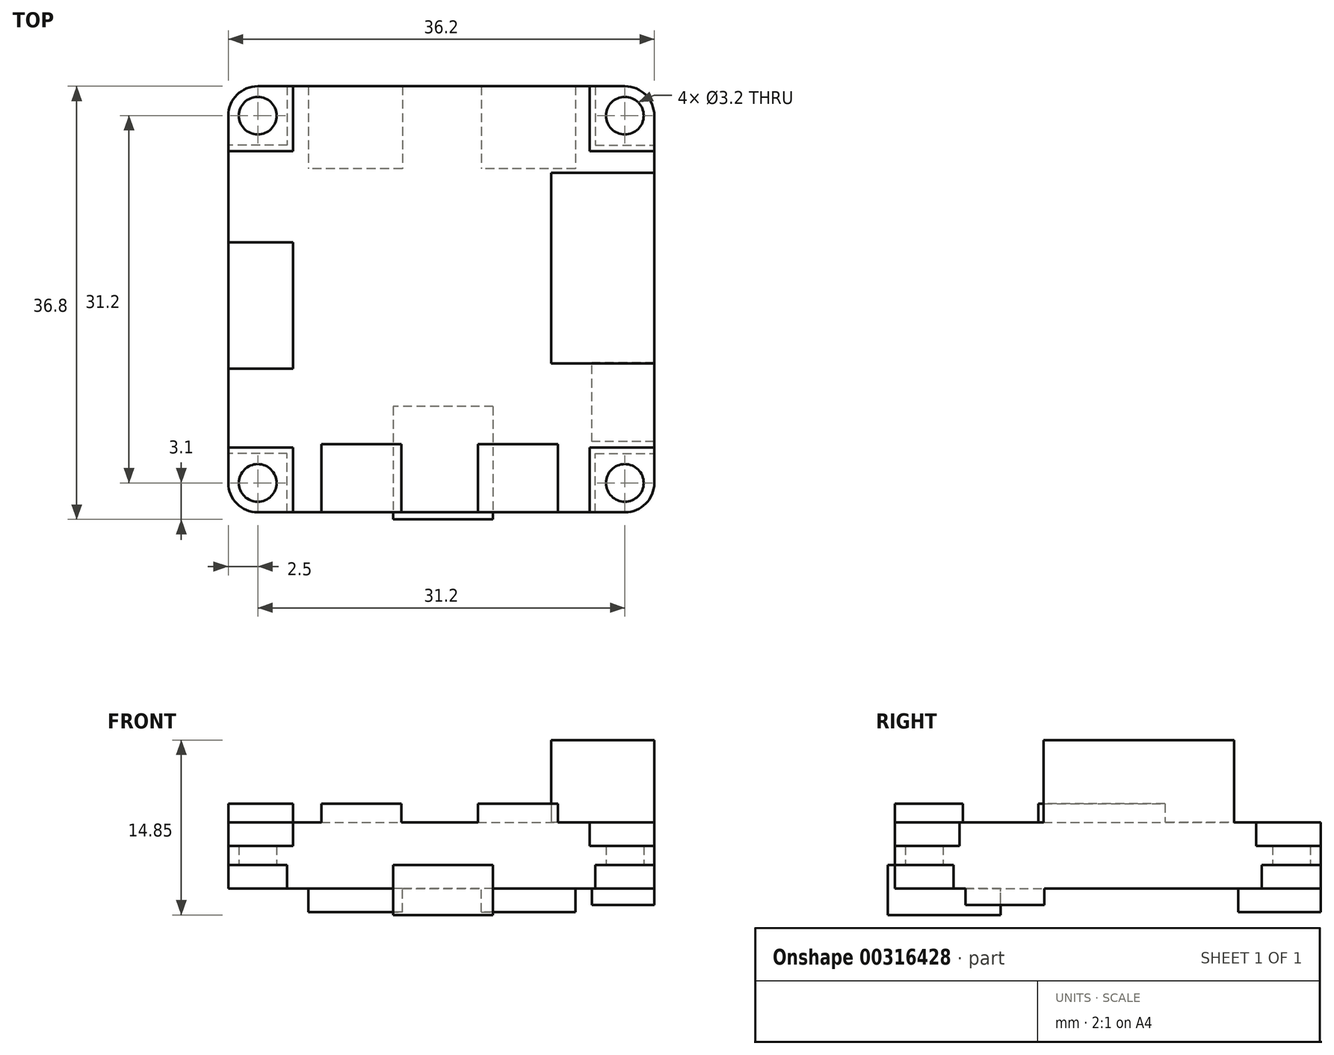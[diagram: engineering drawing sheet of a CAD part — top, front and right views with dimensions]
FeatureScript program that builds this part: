
annotation { "Feature Type Name" : "Feature", "Feature Type Description" : "" }
export const myFeature = defineFeature(function(context is Context, id is Id, definition is map)
    precondition{}
    {
        {
            var Q0;
            Q0=qCreatedBy(makeId("Top.planeOp"),FACE);
            var sketch = newSketch(context, id + "F0", { "sketchPlane" : qUnion([Q0])});
            skLineSegment(sketch, "E0.bottom", {"start": v(-15.6, 18.1) * mm, "end": v(15.6, 18.1) * mm});
            skLineSegment(sketch, "E0.top", {"start": v(-15.6, -18.1) * mm, "end": v(15.6, -18.1) * mm});
            skLineSegment(sketch, "E0.left", {"start": v(-18.1, 15.6) * mm, "end": v(-18.1, -15.6) * mm});
            skLineSegment(sketch, "E0.right", {"start": v(18.1, 15.6) * mm, "end": v(18.1, -15.6) * mm});
            skPoint(sketch, "E0.middle", {"position": v(0, 0) * mm});
            skPoint(sketch, "E1.visualSharp", {"position": v(-18.1, 18.1) * mm});
            skArc(sketch, "E1.filletArc", {"start": v(-15.6, 18.1) * mm, "mid": v(-17.37, 17.37) * mm, "end": v(-18.1, 15.6) * mm});
            skPoint(sketch, "E2.visualSharp", {"position": v(18.1, 18.1) * mm});
            skArc(sketch, "E2.filletArc", {"start": v(18.1, 15.6) * mm, "mid": v(17.37, 17.37) * mm, "end": v(15.6, 18.1) * mm});
            skPoint(sketch, "E3.visualSharp", {"position": v(18.1, -18.1) * mm});
            skArc(sketch, "E3.filletArc", {"start": v(15.6, -18.1) * mm, "mid": v(17.37, -17.37) * mm, "end": v(18.1, -15.6) * mm});
            skPoint(sketch, "E4.visualSharp", {"position": v(-18.1, -18.1) * mm});
            skArc(sketch, "E4.filletArc", {"start": v(-18.1, -15.6) * mm, "mid": v(-17.37, -17.37) * mm, "end": v(-15.6, -18.1) * mm});
            skCircle(sketch, "E5", {"center": v(-15.6, 15.6) * mm, "radius": 1.6 * mm});
            skCircle(sketch, "E6.MirrorC", {"center": v(15.6, 15.6) * mm, "radius": 1.6 * mm});
            skCircle(sketch, "E7.MirrorC", {"center": v(15.6, -15.6) * mm, "radius": 1.6 * mm});
            skCircle(sketch, "E8.MirrorC", {"center": v(-15.6, -15.6) * mm, "radius": 1.6 * mm});
            skSolve(sketch);
        }
        {
            var Q0;
            Q0 = qSketchRegion(id + "F0", true);
            extrude(context, id + "F1", {"entities" : qUnion([Q0]), "depth" : 1.6 * mm});
        }
        {
            var Q0;
            Q0=makeQuery(id+"F1.opExtrude","CAP_FACE",FACE,{"disambiguationData":[OSD([sQuery(id+"F0.wireOp",EDGE,"E0.bottom"),sQuery(id+"F0.wireOp",EDGE,"E0.top"),sQuery(id+"F0.wireOp",EDGE,"E0.left"),sQuery(id+"F0.wireOp",EDGE,"E0.right"),sQuery(id+"F0.wireOp",EDGE,"E1.filletArc"),sQuery(id+"F0.wireOp",EDGE,"E2.filletArc"),sQuery(id+"F0.wireOp",EDGE,"E3.filletArc"),sQuery(id+"F0.wireOp",EDGE,"E4.filletArc"),sQuery(id+"F0.wireOp",EDGE,"E5"),sQuery(id+"F0.wireOp",EDGE,"E6.MirrorC"),sQuery(id+"F0.wireOp",EDGE,"E7.MirrorC"),sQuery(id+"F0.wireOp",EDGE,"E8.MirrorC")])],"isStart":false});
            var sketch = newSketch(context, id + "F2", { "sketchPlane" : qUnion([Q0])});
            skLineSegment(sketch, "E9.bottom", {"start": v(-18.1, -5.9) * mm, "end": v(-12.6, -5.9) * mm});
            skLineSegment(sketch, "E9.top", {"start": v(-18.1, 4.85) * mm, "end": v(-12.6, 4.85) * mm});
            skLineSegment(sketch, "E9.left", {"start": v(-18.1, -5.9) * mm, "end": v(-18.1, 4.85) * mm});
            skLineSegment(sketch, "E9.right", {"start": v(-12.6, -5.9) * mm, "end": v(-12.6, 4.85) * mm});
            skLineSegment(sketch, "E10.bottom", {"start": v(-10.2, -18.1) * mm, "end": v(-3.4, -18.1) * mm});
            skLineSegment(sketch, "E10.top", {"start": v(-10.2, -12.3) * mm, "end": v(-3.4, -12.3) * mm});
            skLineSegment(sketch, "E10.left", {"start": v(-10.2, -18.1) * mm, "end": v(-10.2, -12.3) * mm});
            skLineSegment(sketch, "E10.right", {"start": v(-3.4, -18.1) * mm, "end": v(-3.4, -12.3) * mm});
            skLineSegment(sketch, "E11.bottom", {"start": v(3.1, -18.1) * mm, "end": v(9.9, -18.1) * mm});
            skLineSegment(sketch, "E11.top", {"start": v(3.1, -12.3) * mm, "end": v(9.9, -12.3) * mm});
            skLineSegment(sketch, "E11.left", {"start": v(3.1, -18.1) * mm, "end": v(3.1, -12.3) * mm});
            skLineSegment(sketch, "E11.right", {"start": v(9.9, -18.1) * mm, "end": v(9.9, -12.3) * mm});
            skLineSegment(sketch, "E12.bottom", {"start": v(18.1, -5.46) * mm, "end": v(9.35, -5.46) * mm});
            skLineSegment(sketch, "E12.top", {"start": v(18.1, 10.74) * mm, "end": v(9.35, 10.74) * mm});
            skLineSegment(sketch, "E12.left", {"start": v(18.1, -5.46) * mm, "end": v(18.1, 10.74) * mm});
            skLineSegment(sketch, "E12.right", {"start": v(9.35, -5.46) * mm, "end": v(9.35, 10.74) * mm});
            skLineSegment(sketch, "E13", {"start": v(-18.1, -12.6) * mm, "end": v(-12.6, -12.6) * mm});
            skLineSegment(sketch, "E14", {"start": v(-12.6, -12.6) * mm, "end": v(-12.6, -18.1) * mm});
            skLineSegment(sketch, "E15.MirrorCS", {"start": v(-18.1, 12.6) * mm, "end": v(-12.6, 12.6) * mm});
            skLineSegment(sketch, "E16.MirrorCS", {"start": v(-12.6, 12.6) * mm, "end": v(-12.6, 18.1) * mm});
            skLineSegment(sketch, "E17.MirrorCS", {"start": v(12.6, 12.6) * mm, "end": v(12.6, 18.1) * mm});
            skLineSegment(sketch, "E18.MirrorCS", {"start": v(18.1, 12.6) * mm, "end": v(12.6, 12.6) * mm});
            skLineSegment(sketch, "E19.MirrorCS", {"start": v(12.6, -12.6) * mm, "end": v(12.6, -18.1) * mm});
            skLineSegment(sketch, "E20.MirrorCS", {"start": v(18.1, -12.6) * mm, "end": v(12.6, -12.6) * mm});
            skSolve(sketch);
        }
        {
            var Q0;
            Q0=makeQuery(id+"F2.imprint","IMPRINT",FACE,{"disambiguationData":[TD([[makeQuery(id+"F2.imprint","IMPRINT",EDGE,{"derivedFrom":sQuery(id+"F2.wireOp",EDGE,"E9.bottom")}),1.0]])]});
            var Q1;
            Q1=makeQuery(id+"F2.imprint","IMPRINT",FACE,{"disambiguationData":[TD([[makeQuery(id+"F2.imprint","IMPRINT",EDGE,{"derivedFrom":sQuery(id+"F2.wireOp",EDGE,"E10.bottom")}),1.0]])]});
            var Q2;
            Q2=makeQuery(id+"F2.imprint","IMPRINT",FACE,{"disambiguationData":[TD([[makeQuery(id+"F2.imprint","IMPRINT",EDGE,{"derivedFrom":sQuery(id+"F2.wireOp",EDGE,"E11.bottom")}),1.0]])]});
            extrude(context, id + "F3", {"entities" : qUnion([Q0, Q1, Q2]), "operationType" : NewBodyOperationType.ADD, "depth" : 3.6 * mm});
        }
        {
            var Q0;
            Q0=makeQuery(id+"F2.imprint","IMPRINT",FACE,{"disambiguationData":[TD([[makeQuery(id+"F2.imprint","IMPRINT",EDGE,{"derivedFrom":sQuery(id+"F2.wireOp",EDGE,"E12.bottom")}),-1.0]])]});
            extrude(context, id + "F4", {"entities" : qUnion([Q0]), "operationType" : NewBodyOperationType.ADD, "depth" : 9 * mm});
        }
        {
            var Q0;
            {var subQ14=sQuery(id+"F2.wireOp",EDGE,"E9.bottom");Q0=makeQuery(id+"F2.imprint","IMPRINT",FACE,{"disambiguationData":[TD([[makeQuery(id+"F2.imprint","IMPRINT",EDGE,{"derivedFrom":subQ14}),-1.0]])]});}
            extrude(context, id + "F5", {"entities" : qUnion([Q0]), "operationType" : NewBodyOperationType.ADD, "depth" : 2 * mm});
        }
        {
            var Q0;
            Q0=makeQuery(id+"F1.opExtrude","CAP_FACE",FACE,{"disambiguationData":[OSD([sQuery(id+"F0.wireOp",EDGE,"E0.bottom"),sQuery(id+"F0.wireOp",EDGE,"E0.top"),sQuery(id+"F0.wireOp",EDGE,"E0.left"),sQuery(id+"F0.wireOp",EDGE,"E0.right"),sQuery(id+"F0.wireOp",EDGE,"E1.filletArc"),sQuery(id+"F0.wireOp",EDGE,"E2.filletArc"),sQuery(id+"F0.wireOp",EDGE,"E3.filletArc"),sQuery(id+"F0.wireOp",EDGE,"E4.filletArc"),sQuery(id+"F0.wireOp",EDGE,"E5"),sQuery(id+"F0.wireOp",EDGE,"E6.MirrorC"),sQuery(id+"F0.wireOp",EDGE,"E7.MirrorC"),sQuery(id+"F0.wireOp",EDGE,"E8.MirrorC")])],"isStart":true});
            var sketch = newSketch(context, id + "F6", { "sketchPlane" : qUnion([Q0])});
            skLineSegment(sketch, "E21.bottom", {"start": v(18.1, 12.1) * mm, "end": v(12.8, 12.1) * mm});
            skLineSegment(sketch, "E21.top", {"start": v(18.1, 5.4) * mm, "end": v(12.8, 5.4) * mm});
            skLineSegment(sketch, "E21.left", {"start": v(18.1, 12.1) * mm, "end": v(18.1, 5.4) * mm});
            skLineSegment(sketch, "E21.right", {"start": v(12.8, 12.1) * mm, "end": v(12.8, 5.4) * mm});
            skLineSegment(sketch, "E22.bottom", {"start": v(11.4, -18.1) * mm, "end": v(3.4, -18.1) * mm});
            skLineSegment(sketch, "E22.top", {"start": v(11.4, -11.1) * mm, "end": v(3.4, -11.1) * mm});
            skLineSegment(sketch, "E22.left", {"start": v(11.4, -18.1) * mm, "end": v(11.4, -11.1) * mm});
            skLineSegment(sketch, "E22.right", {"start": v(3.4, -18.1) * mm, "end": v(3.4, -11.1) * mm});
            skLineSegment(sketch, "E23.bottom", {"start": v(-3.3, -18.1) * mm, "end": v(-11.3, -18.1) * mm});
            skLineSegment(sketch, "E23.top", {"start": v(-3.3, -11.1) * mm, "end": v(-11.3, -11.1) * mm});
            skLineSegment(sketch, "E23.left", {"start": v(-3.3, -18.1) * mm, "end": v(-3.3, -11.1) * mm});
            skLineSegment(sketch, "E23.right", {"start": v(-11.3, -18.1) * mm, "end": v(-11.3, -11.1) * mm});
            skLineSegment(sketch, "E24.bottom", {"start": v(4.4, 9.1) * mm, "end": v(-4.1, 9.1) * mm});
            skLineSegment(sketch, "E24.top", {"start": v(4.4, 18.7) * mm, "end": v(-4.1, 18.7) * mm});
            skLineSegment(sketch, "E24.left", {"start": v(4.4, 9.1) * mm, "end": v(4.4, 18.7) * mm});
            skLineSegment(sketch, "E24.right", {"start": v(-4.1, 9.1) * mm, "end": v(-4.1, 18.7) * mm});
            skLineSegment(sketch, "E25", {"start": v(-13.1, -18.1) * mm, "end": v(-13.1, -13.1) * mm});
            skLineSegment(sketch, "E26", {"start": v(-13.1, -13.1) * mm, "end": v(-18.1, -13.1) * mm});
            skLineSegment(sketch, "E27.MirrorCS", {"start": v(13.1, -13.1) * mm, "end": v(18.1, -13.1) * mm});
            skLineSegment(sketch, "E28.MirrorCS", {"start": v(13.1, -18.1) * mm, "end": v(13.1, -13.1) * mm});
            skLineSegment(sketch, "E29.MirrorCS", {"start": v(13.1, 13.1) * mm, "end": v(18.1, 13.1) * mm});
            skLineSegment(sketch, "E30.MirrorCS", {"start": v(13.1, 18.1) * mm, "end": v(13.1, 13.1) * mm});
            skLineSegment(sketch, "E31.MirrorCS", {"start": v(-13.1, 13.1) * mm, "end": v(-18.1, 13.1) * mm});
            skLineSegment(sketch, "E32.MirrorCS", {"start": v(-13.1, 18.1) * mm, "end": v(-13.1, 13.1) * mm});
            skSolve(sketch);
        }
        {
            var Q0;
            {var subQ23=sQuery(id+"F6.wireOp",EDGE,"E21.bottom");Q0=makeQuery(id+"F6.imprint","IMPRINT",FACE,{"disambiguationData":[TD([[makeQuery(id+"F6.imprint","IMPRINT",EDGE,{"derivedFrom":subQ23}),-1.0]])]});}
            extrude(context, id + "F7", {"entities" : qUnion([Q0]), "operationType" : NewBodyOperationType.ADD, "depth" : 2 * mm});
        }
        {
            var Q0;
            {var subQ0=sQuery(id+"F6.wireOp",EDGE,"E24.top");Q0=makeQuery(id+"F6.imprint","IMPRINT",FACE,{"disambiguationData":[TD([[makeQuery(id+"F6.imprint","IMPRINT",EDGE,{"derivedFrom":subQ0}),1.0]])]});}
            var Q1;
            {var subQ0=sQuery(id+"F6.wireOp",EDGE,"E24.bottom");Q1=makeQuery(id+"F6.imprint","IMPRINT",FACE,{"disambiguationData":[TD([[makeQuery(id+"F6.imprint","IMPRINT",EDGE,{"derivedFrom":subQ0}),-1.0]])]});}
            extrude(context, id + "F8", {"entities" : qUnion([Q0, Q1]), "operationType" : NewBodyOperationType.ADD, "depth" : 4.25 * mm});
        }
        {
            var Q0;
            Q0=makeQuery(id+"F6.imprint","IMPRINT",FACE,{"disambiguationData":[TD([[makeQuery(id+"F6.imprint","IMPRINT",EDGE,{"derivedFrom":sQuery(id+"F6.wireOp",EDGE,"E21.bottom")}),1.0]])]});
            extrude(context, id + "F9", {"entities" : qUnion([Q0]), "operationType" : NewBodyOperationType.ADD, "depth" : 3.4 * mm});
        }
        {
            var Q0;
            Q0=makeQuery(id+"F6.imprint","IMPRINT",FACE,{"disambiguationData":[TD([[makeQuery(id+"F6.imprint","IMPRINT",EDGE,{"derivedFrom":sQuery(id+"F6.wireOp",EDGE,"E22.bottom")}),1.0]])]});
            var Q1;
            Q1=makeQuery(id+"F6.imprint","IMPRINT",FACE,{"disambiguationData":[TD([[makeQuery(id+"F6.imprint","IMPRINT",EDGE,{"derivedFrom":sQuery(id+"F6.wireOp",EDGE,"E23.bottom")}),1.0]])]});
            extrude(context, id + "F10", {"entities" : qUnion([Q0, Q1]), "operationType" : NewBodyOperationType.ADD, "depth" : 4 * mm});
        }
    });
